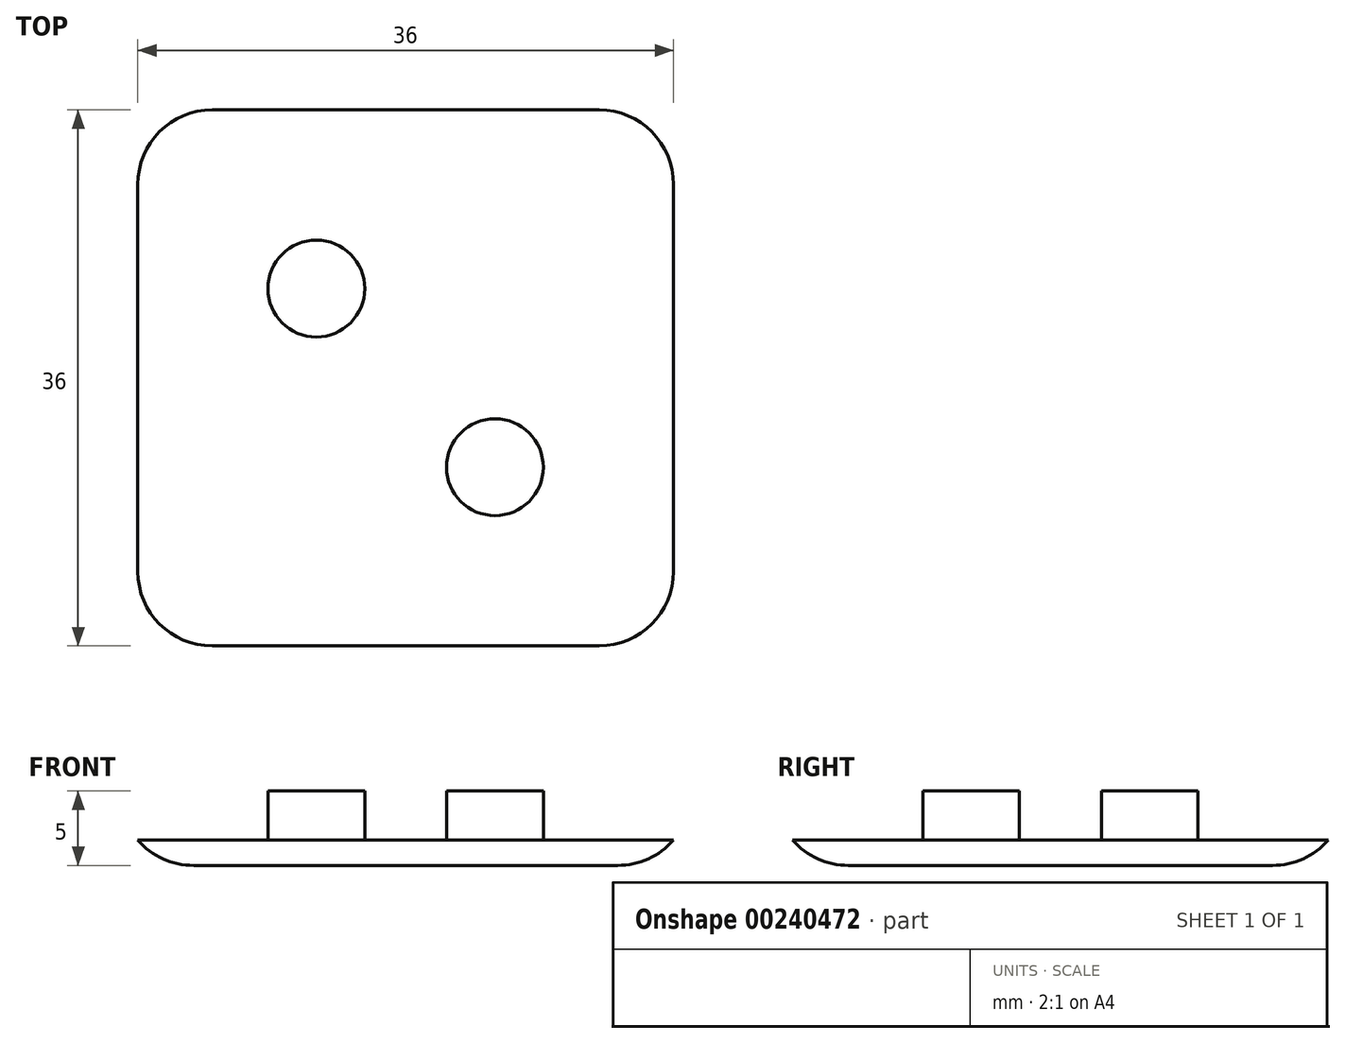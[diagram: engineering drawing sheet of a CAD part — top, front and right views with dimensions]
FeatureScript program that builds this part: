
annotation { "Feature Type Name" : "Feature", "Feature Type Description" : "" }
export const myFeature = defineFeature(function(context is Context, id is Id, definition is map)
    precondition{}
    {
        {
            var Q0;
            Q0=qCreatedBy(makeId("Top.planeOp"),FACE);
            var sketch = newSketch(context, id + "F0", { "sketchPlane" : qUnion([Q0])});
            skLineSegment(sketch, "E0.bottom", {"start": v(18, 18) * mm, "end": v(-18, 18) * mm});
            skLineSegment(sketch, "E0.top", {"start": v(18, -18) * mm, "end": v(-18, -18) * mm});
            skLineSegment(sketch, "E0.left", {"start": v(18, 18) * mm, "end": v(18, -18) * mm});
            skLineSegment(sketch, "E0.right", {"start": v(-18, 18) * mm, "end": v(-18, -18) * mm});
            skPoint(sketch, "E0.middle", {"position": v(0, 0) * mm});
            skSolve(sketch);
        }
        {
            var Q0;
            Q0=makeQuery(id+"F0.imprint","IMPRINT",FACE,{"disambiguationData":[TD([[makeQuery(id+"F0.imprint","IMPRINT",EDGE,{"derivedFrom":sQuery(id+"F0.wireOp",EDGE,"E0.bottom")}),1.0]])]});
            extrude(context, id + "F1", {"entities" : qUnion([Q0]), "endBound" : BoundingType.SYMMETRIC, "depth" : 5 * mm});
        }
        {
            var Q0;
            Q0=makeQuery(id+"F1.opExtrude","CAP_FACE",FACE,{"disambiguationData":[OSD([sQuery(id+"F0.wireOp",EDGE,"E0.bottom"),sQuery(id+"F0.wireOp",EDGE,"E0.top"),sQuery(id+"F0.wireOp",EDGE,"E0.left"),sQuery(id+"F0.wireOp",EDGE,"E0.right")])],"isStart":false});
            var sketch = newSketch(context, id + "F2", { "sketchPlane" : qUnion([Q0])});
            skPoint(sketch, "E1.middle", {"position": v(0, 0) * mm});
            skCircle(sketch, "E2", {"center": v(6, 6) * mm, "radius": 3.25 * mm});
            skCircle(sketch, "E3.MirrorC", {"center": v(-6, 6) * mm, "radius": 3.25 * mm});
            skCircle(sketch, "E4.MirrorC", {"center": v(-6, -6) * mm, "radius": 3.25 * mm});
            skCircle(sketch, "E5.MirrorC", {"center": v(6, -6) * mm, "radius": 3.25 * mm});
            skSolve(sketch);
        }
        {
            var Q0;
            Q0=makeQuery(id+"F2.imprint","IMPRINT",FACE,{"disambiguationData":[TD([[makeQuery(id+"F2.imprint","IMPRINT",EDGE,{"derivedFrom":sQuery(id+"F2.wireOp",EDGE,"E3.MirrorC")}),-1.0]])]});
            var Q1;
            Q1=makeQuery(id+"F2.imprint","IMPRINT",FACE,{"disambiguationData":[TD([[makeQuery(id+"F2.imprint","IMPRINT",EDGE,{"derivedFrom":sQuery(id+"F2.wireOp",EDGE,"E2")}),1.0]])]});
            var Q2;
            Q2=makeQuery(id+"F2.imprint","IMPRINT",FACE,{"disambiguationData":[TD([[makeQuery(id+"F2.imprint","IMPRINT",EDGE,{"derivedFrom":sQuery(id+"F2.wireOp",EDGE,"E5.MirrorC")}),-1.0]])]});
            var Q3;
            Q3=makeQuery(id+"F2.imprint","IMPRINT",FACE,{"disambiguationData":[TD([[makeQuery(id+"F2.imprint","IMPRINT",EDGE,{"derivedFrom":sQuery(id+"F2.wireOp",EDGE,"E4.MirrorC")}),1.0]])]});
            extrude(context, id + "F3", {"entities" : qUnion([Q0, Q1, Q2, Q3]), "operationType" : NewBodyOperationType.REMOVE, "oppositeDirection" : true, "depth" : 3.3 * mm});
        }
        {
            var Q0;
            Q0=makeQuery(id+"F1.opExtrude","SWEPT_EDGE",EDGE,{"disambiguationData":[OSD([sQuery(id+"F0.wireOp",EDGE,"E0.top"),sQuery(id+"F0.wireOp",EDGE,"E0.right")])]});
            var Q1;
            Q1=makeQuery(id+"F1.opExtrude","SWEPT_EDGE",EDGE,{"disambiguationData":[OSD([sQuery(id+"F0.wireOp",EDGE,"E0.bottom"),sQuery(id+"F0.wireOp",EDGE,"E0.right")])]});
            var Q2;
            Q2=makeQuery(id+"F1.opExtrude","SWEPT_EDGE",EDGE,{"disambiguationData":[OSD([sQuery(id+"F0.wireOp",EDGE,"E0.top"),sQuery(id+"F0.wireOp",EDGE,"E0.left")])]});
            var Q3;
            Q3=makeQuery(id+"F1.opExtrude","SWEPT_EDGE",EDGE,{"disambiguationData":[OSD([sQuery(id+"F0.wireOp",EDGE,"E0.bottom"),sQuery(id+"F0.wireOp",EDGE,"E0.left")])]});
            fillet(context, id + "F4", {"entities" : qUnion([Q0, Q1, Q2, Q3]), "radius" : 5 * mm, "tangentPropagation" : true, "allowEdgeOverflow" : false});
        }
        {
            var Q0;
            Q0=makeQuery(id+"F1.opExtrude","CAP_EDGE",EDGE,{"disambiguationData":[OSD([sQuery(id+"F0.wireOp",EDGE,"E0.bottom")])],"isStart":true});
            fillet(context, id + "F5", {"entities" : qUnion([Q0]), "radius" : 5 * mm, "tangentPropagation" : true, "allowEdgeOverflow" : false});
        }
    });
